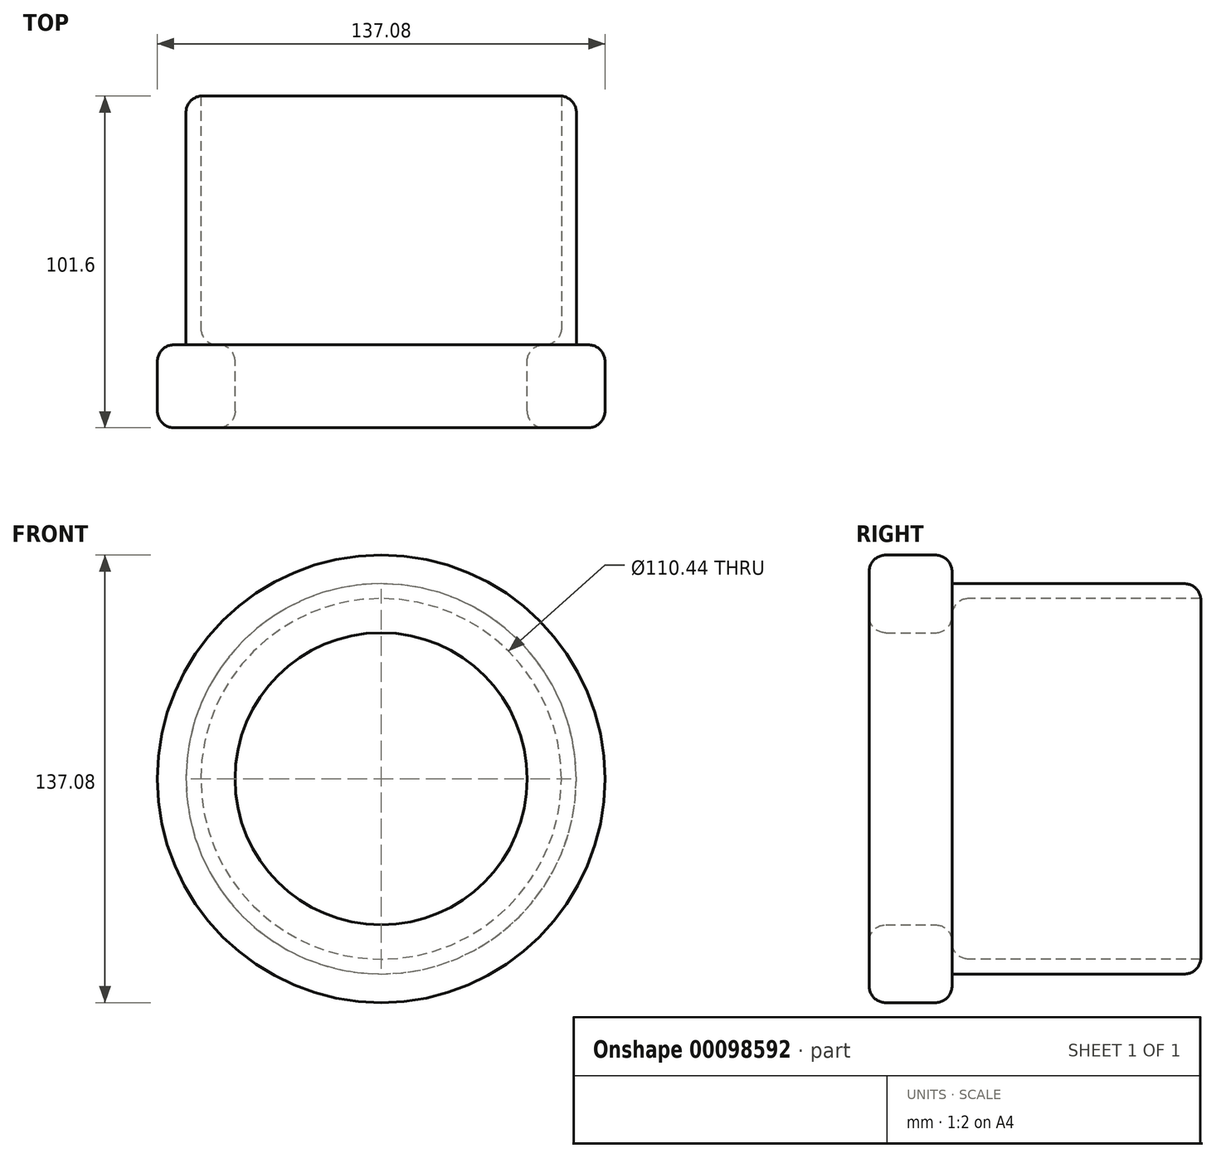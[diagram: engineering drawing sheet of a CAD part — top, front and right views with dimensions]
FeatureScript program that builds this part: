
annotation { "Feature Type Name" : "Feature", "Feature Type Description" : "" }
export const myFeature = defineFeature(function(context is Context, id is Id, definition is map)
    precondition{}
    {
        {
            var Q0;
            Q0=qCreatedBy(makeId("Front.planeOp"),FACE);
            var sketch = newSketch(context, id + "F0", { "sketchPlane" : qUnion([Q0])});
            skCircle(sketch, "E0", {"center": v(0, 0) * mm, "radius": 44.73 * mm});
            skCircle(sketch, "E1", {"center": v(0, 0) * mm, "radius": 68.54 * mm});
            skSolve(sketch);
        }
        {
            var Q0;
            Q0=makeQuery(id+"F0.imprint","IMPRINT",FACE,{"disambiguationData":[TD([[makeQuery(id+"F0.imprint","IMPRINT",EDGE,{"derivedFrom":sQuery(id+"F0.wireOp",EDGE,"E0")}),-1.0]])]});
            extrude(context, id + "F1", {"entities" : qUnion([Q0]), "depth" : 25.4 * mm});
        }
        {
            var Q0;
            Q0=makeQuery(id+"F1.opExtrude","CAP_EDGE",EDGE,{"disambiguationData":[OSD([sQuery(id+"F0.wireOp",EDGE,"E1")])],"isStart":false});
            var Q1;
            Q1=makeQuery(id+"F1.opExtrude","SWEPT_FACE",FACE,{"disambiguationData":[OSD([sQuery(id+"F0.wireOp",EDGE,"E1")])]});
            var Q2;
            Q2=makeQuery(id+"F1.opExtrude","CAP_FACE",FACE,{"disambiguationData":[OSD([sQuery(id+"F0.wireOp",EDGE,"E0"),sQuery(id+"F0.wireOp",EDGE,"E1")])],"isStart":false});
            var Q3;
            Q3=makeQuery(id+"F1.opExtrude","SWEPT_FACE",FACE,{"disambiguationData":[OSD([sQuery(id+"F0.wireOp",EDGE,"E0")])]});
            fillet(context, id + "F2", {"entities" : qUnion([Q0, Q1, Q2, Q3]), "radius" : 5.08 * mm, "tangentPropagation" : true, "allowEdgeOverflow" : false});
        }
        {
            var Q0;
            Q0=qCreatedBy(makeId("Front.planeOp"),FACE);
            var sketch = newSketch(context, id + "F3", { "sketchPlane" : qUnion([Q0])});
            skCircle(sketch, "E2", {"center": v(0, 0) * mm, "radius": 59.78 * mm});
            skCircle(sketch, "E3", {"center": v(0, 0) * mm, "radius": 55.22 * mm});
            skSolve(sketch);
        }
        {
            var Q0;
            Q0 = qSketchRegion(id + "F3", true);
            extrude(context, id + "F4", {"entities" : qUnion([Q0]), "operationType" : NewBodyOperationType.ADD, "oppositeDirection" : true, "depth" : 76.2 * mm});
        }
        {
            var Q0;
            Q0=makeQuery(id+"F4.opExtrude","CAP_EDGE",EDGE,{"disambiguationData":[OSD([sQuery(id+"F3.wireOp",EDGE,"E2")])],"isStart":false});
            var Q1;
            Q1=makeQuery(id+"F4.opExtrude","CAP_EDGE",EDGE,{"disambiguationData":[OSD([sQuery(id+"F3.wireOp",EDGE,"E2")])],"isStart":true});
            var Q2;
            Q2=makeQuery(id+"F4.opExtrude","CAP_EDGE",EDGE,{"disambiguationData":[OSD([sQuery(id+"F3.wireOp",EDGE,"E3")])],"isStart":true});
            fillet(context, id + "F5", {"entities" : qUnion([Q0, Q1, Q2]), "radius" : 5.08 * mm, "tangentPropagation" : true, "allowEdgeOverflow" : false});
        }
    });
